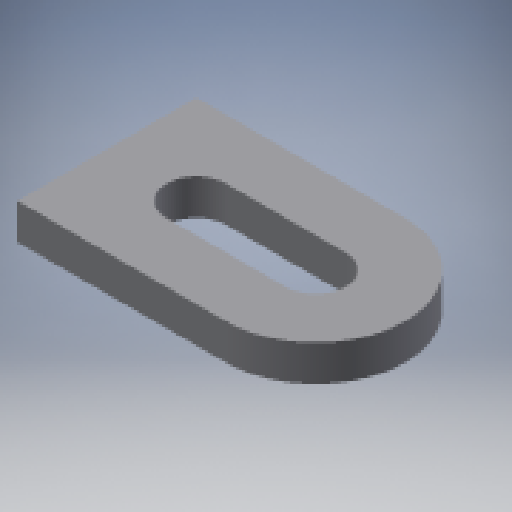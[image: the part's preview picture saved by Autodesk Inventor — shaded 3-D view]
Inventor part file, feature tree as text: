
AUTODESK INVENTOR PART (.ipt)
format: ipt  version: 2024.3 (Build 283343000, 343)  size: 228,864 bytes
history: native  units: mm
features: extrude x2, fillet x1, sketch x1
ambient origin geometry x8: Origin, YZ Plane, XZ Plane, XY Plane, X Axis, Y Axis, Z Axis, Center Point
bodies: Volumenkörper1 (feature_tree)
feature tree (4):
  extrude  "Extrusion1"  Depth=10.0mm
  fillet  "Rundung1"  Radius=2.0mm
  extrude  "Extrusion2"  Depth=7.5mm
  sketch  "Skizze2"  dims[d0=15.0mm d1=25.0mm d2=2.0mm d3=0.0mm d4=7.5mm d5=4.5mm d6=10.0mm d7=0.0mm d8=0.0mm]
